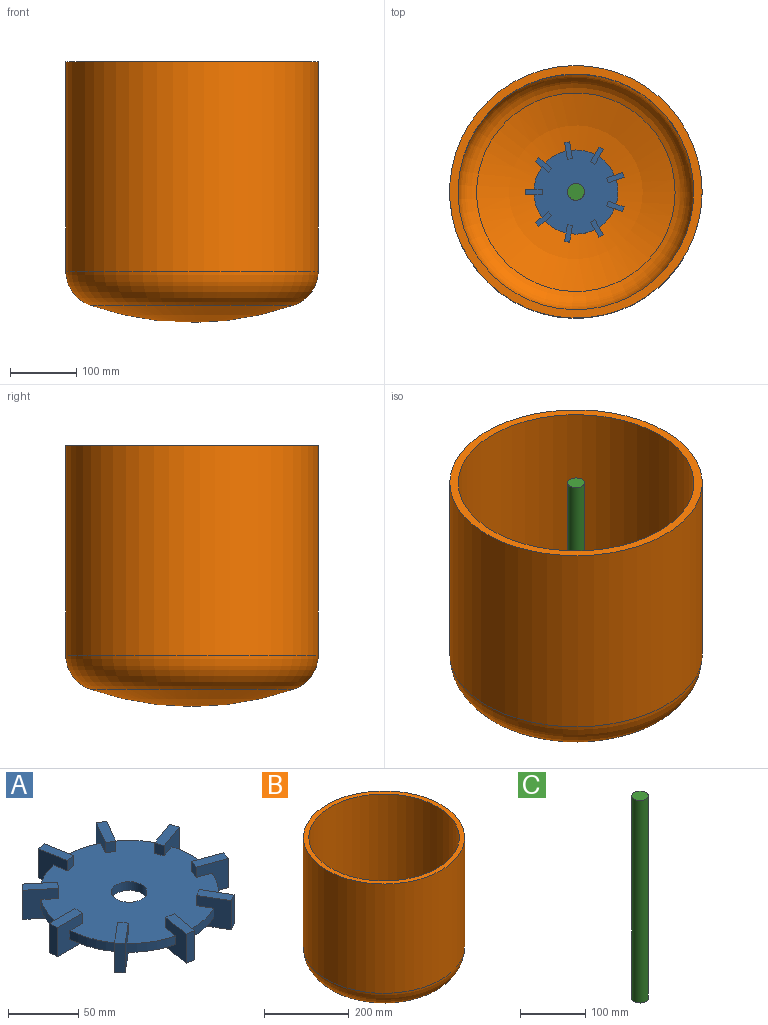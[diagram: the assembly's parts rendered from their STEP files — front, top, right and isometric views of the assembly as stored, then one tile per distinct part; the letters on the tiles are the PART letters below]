
ASSEMBLY  parts=3 mates=2
PART A: 75 faces, bbox 149.1x151.4x25.4 mm
  f0: cylinder r=63.5mm len=34.02mm, axis (0,0,-1), area 279.7mm2, adj f1,f2,f16,f70
  f1: plane 127x126.89mm, normal (0,0,1), area 11292.6mm2, adj f0,f3,f4,f5,f6,f7,f8,f9
  f2: plane 127x126.89mm, normal (0,0,-1), area 11292.6mm2, adj f0,f3,f4,f5,f6,f7,f8,f9
  f3: cylinder r=63.5mm len=31.35mm, axis (0,0,-1), area 279.7mm2, adj f1,f2,f63,f72
  f4: cylinder r=63.5mm len=35.65mm, axis (0,0,-1), area 279.7mm2, adj f1,f2,f56,f65
  f5: cylinder r=63.5mm len=27.73mm, axis (0,0,-1), area 279.7mm2, adj f1,f2,f49,f58
  f6: cylinder r=63.5mm len=36.2mm, axis (0,0,-1), area 279.7mm2, adj f1,f2,f42,f51
  f7: cylinder r=63.5mm len=27.73mm, axis (0,0,-1), area 279.7mm2, adj f1,f2,f35,f44
  f8: cylinder r=63.5mm len=35.65mm, axis (0,0,-1), area 279.7mm2, adj f1,f2,f28,f37
  f9: cylinder r=63.5mm len=31.35mm, axis (0,0,-1), area 279.7mm2, adj f1,f2,f21,f30
  f10: cylinder r=63.5mm len=34.02mm, axis (0,0,-1), area 279.7mm2, adj f1,f2,f14,f23
  f11: cylinder r=12.7mm len=25.4mm, axis (0,0,-1), area 608mm2, adj f1,f2
  f12: plane 8.89x7.62mm, normal (1,0,0), area 67.7mm2, adj f2,f14,f16,f18
  f13: plane 25.4x7.62mm, normal (-1,0,0), area 193.5mm2, adj f14,f16,f17,f18
  f14: plane 25.4x25.4mm, normal (0,-1,0), area 549.3mm2, adj f1,f2,f10,f12,f13,f15,f17,f18
  f15: plane 8.89x7.62mm, normal (1,0,0), area 67.7mm2, adj f1,f14,f16,f17
  f16: plane 25.4x25.4mm, normal (0,1,0), area 549.3mm2, adj f0,f1,f2,f12,f13,f15,f17,f18
  f17: plane 25.4x7.62mm, normal (0,0,1), area 193.5mm2, adj f13,f14,f15,f16
  f18: plane 25.4x7.62mm, normal (0,0,-1), area 193.5mm2, adj f12,f13,f14,f16
  f19: plane 8.89x5.84mm, normal (0.77,0.64,0), area 67.7mm2, adj f2,f21,f23,f25
  f20: plane 25.4x5.84mm, normal (-0.77,-0.64,0), area 193.5mm2, adj f21,f23,f24,f25
  f21: plane 25.4x19.46mm, normal (0.64,-0.77,0), area 549.3mm2, adj f1,f2,f9,f19,f20,f22,f24,f25
  f22: plane 8.89x5.84mm, normal (0.77,0.64,0), area 67.7mm2, adj f1,f21,f23,f24
  f23: plane 25.4x19.46mm, normal (-0.64,0.77,0), area 549.3mm2, adj f1,f2,f10,f19,f20,f22,f24,f25
  f24: plane 24.36x22.16mm, normal (0,0,1), area 193.5mm2, adj f20,f21,f22,f23
  f25: plane 24.36x22.16mm, normal (0,0,-1), area 193.5mm2, adj f19,f20,f21,f23
  f26: plane 8.89x7.5mm, normal (0.17,0.98,0), area 67.7mm2, adj f2,f28,f30,f32
  f27: plane 25.4x7.5mm, normal (-0.17,-0.98,0), area 193.5mm2, adj f28,f30,f31,f32
  f28: plane 25.4x25.01mm, normal (0.98,-0.17,0), area 549.3mm2, adj f1,f2,f8,f26,f27,f29,f31,f32
  f29: plane 8.89x7.5mm, normal (0.17,0.98,0), area 67.7mm2, adj f1,f28,f30,f31
  f30: plane 25.4x25.01mm, normal (-0.98,0.17,0), area 549.3mm2, adj f1,f2,f9,f26,f27,f29,f31,f32
  f31: plane 26.34x11.92mm, normal (0,0,1), area 193.5mm2, adj f27,f28,f29,f30
  f32: plane 26.34x11.92mm, normal (0,0,-1), area 193.5mm2, adj f26,f27,f28,f30
  f33: plane 8.89x6.6mm, normal (-0.5,0.87,0), area 67.7mm2, adj f2,f35,f37,f39
  f34: plane 25.4x6.6mm, normal (0.5,-0.87,0), area 193.5mm2, adj f35,f37,f38,f39
  f35: plane 25.4x22mm, normal (0.87,0.5,0), area 549.3mm2, adj f1,f2,f7,f33,f34,f36,f38,f39
  f36: plane 8.89x6.6mm, normal (-0.5,0.87,0), area 67.7mm2, adj f1,f35,f37,f38
  f37: plane 25.4x22mm, normal (-0.87,-0.5,0), area 549.3mm2, adj f1,f2,f8,f33,f34,f36,f38,f39
  f38: plane 25.81x19.3mm, normal (0,0,1), area 193.5mm2, adj f34,f35,f36,f37
  f39: plane 25.81x19.3mm, normal (0,0,-1), area 193.5mm2, adj f33,f34,f35,f37
  f40: plane 8.89x7.16mm, normal (-0.94,0.34,0), area 67.7mm2, adj f2,f42,f44,f46
  f41: plane 25.4x7.16mm, normal (0.94,-0.34,0), area 193.5mm2, adj f42,f44,f45,f46
  f42: plane 25.4x23.87mm, normal (0.34,0.94,0), area 549.3mm2, adj f1,f2,f6,f40,f41,f43,f45,f46
  f43: plane 8.89x7.16mm, normal (-0.94,0.34,0), area 67.7mm2, adj f1,f42,f44,f45
  f44: plane 25.4x23.87mm, normal (-0.34,-0.94,0), area 549.3mm2, adj f1,f2,f7,f40,f41,f43,f45,f46
  f45: plane 26.47x15.85mm, normal (0,0,1), area 193.5mm2, adj f41,f42,f43,f44
  f46: plane 26.47x15.85mm, normal (0,0,-1), area 193.5mm2, adj f40,f41,f42,f44
  f47: plane 8.89x7.16mm, normal (-0.94,-0.34,0), area 67.7mm2, adj f2,f49,f51,f53
  f48: plane 25.4x7.16mm, normal (0.94,0.34,0), area 193.5mm2, adj f49,f51,f52,f53
  f49: plane 25.4x23.87mm, normal (-0.34,0.94,0), area 549.3mm2, adj f1,f2,f5,f47,f48,f50,f52,f53
  f50: plane 8.89x7.16mm, normal (-0.94,-0.34,0), area 67.7mm2, adj f1,f49,f51,f52
  f51: plane 25.4x23.87mm, normal (0.34,-0.94,0), area 549.3mm2, adj f1,f2,f6,f47,f48,f50,f52,f53
  f52: plane 26.47x15.85mm, normal (0,0,1), area 193.5mm2, adj f48,f49,f50,f51
  f53: plane 26.47x15.85mm, normal (0,0,-1), area 193.5mm2, adj f47,f48,f49,f51
  f54: plane 8.89x6.6mm, normal (-0.5,-0.87,0), area 67.7mm2, adj f2,f56,f58,f60
  f55: plane 25.4x6.6mm, normal (0.5,0.87,0), area 193.5mm2, adj f56,f58,f59,f60
  f56: plane 25.4x22mm, normal (-0.87,0.5,0), area 549.3mm2, adj f1,f2,f4,f54,f55,f57,f59,f60
  f57: plane 8.89x6.6mm, normal (-0.5,-0.87,0), area 67.7mm2, adj f1,f56,f58,f59
  f58: plane 25.4x22mm, normal (0.87,-0.5,0), area 549.3mm2, adj f1,f2,f5,f54,f55,f57,f59,f60
  f59: plane 25.81x19.3mm, normal (0,0,1), area 193.5mm2, adj f55,f56,f57,f58
  f60: plane 25.81x19.3mm, normal (0,0,-1), area 193.5mm2, adj f54,f55,f56,f58
  f61: plane 8.89x7.5mm, normal (0.17,-0.98,0), area 67.7mm2, adj f2,f63,f65,f67
  f62: plane 25.4x7.5mm, normal (-0.17,0.98,0), area 193.5mm2, adj f63,f65,f66,f67
  f63: plane 25.4x25.01mm, normal (-0.98,-0.17,0), area 549.3mm2, adj f1,f2,f3,f61,f62,f64,f66,f67
  f64: plane 8.89x7.5mm, normal (0.17,-0.98,0), area 67.7mm2, adj f1,f63,f65,f66
  f65: plane 25.4x25.01mm, normal (0.98,0.17,0), area 549.3mm2, adj f1,f2,f4,f61,f62,f64,f66,f67
  f66: plane 26.34x11.92mm, normal (0,0,1), area 193.5mm2, adj f62,f63,f64,f65
  f67: plane 26.34x11.92mm, normal (0,0,-1), area 193.5mm2, adj f61,f62,f63,f65
  f68: plane 8.89x5.84mm, normal (0.77,-0.64,0), area 67.7mm2, adj f2,f70,f72,f74
  f69: plane 25.4x5.84mm, normal (-0.77,0.64,0), area 193.5mm2, adj f70,f72,f73,f74
  f70: plane 25.4x19.46mm, normal (-0.64,-0.77,0), area 549.3mm2, adj f0,f1,f2,f68,f69,f71,f73,f74
  f71: plane 8.89x5.84mm, normal (0.77,-0.64,0), area 67.7mm2, adj f1,f70,f72,f73
  f72: plane 25.4x19.46mm, normal (0.64,0.77,0), area 549.3mm2, adj f1,f2,f3,f68,f69,f71,f73,f74
  f73: plane 24.36x22.16mm, normal (0,0,1), area 193.5mm2, adj f69,f70,f71,f72
  f74: plane 24.36x22.16mm, normal (0,0,-1), area 193.5mm2, adj f68,f69,f70,f72
PART B: 7 faces, bbox 412.4x412.4x393.7 mm
  f0: sphere r=468.63mm, area 76527.2mm2, adj f6
  f1: sphere r=455.93mm, area 72435.6mm2, adj f2
  f2: torus R=136mm, axis (0,0,1), area 54527.9mm2, adj f1,f3
  f3: cylinder r=177.8mm len=355.6mm, axis (0,0,1), area 353276.5mm2, adj f2,f4
  f4: plane 381x381mm, normal (0,0,1), area 14694.5mm2, adj f3,f5
  f5: cylinder r=190.5mm len=381mm, axis (0,0,1), area 378510.5mm2, adj f4,f6
  f6: torus R=136mm, axis (0,0,1), area 75201.8mm2, adj f0,f5
PART C: 3 faces, bbox 25.4x25.4x381 mm
  f0: cylinder r=12.7mm len=381mm, axis (0,0,-1), area 30402.4mm2, adj f1,f2
  f1: plane 25.4x25.4mm, normal (0,0,1), area 506.7mm2, adj f0
  f2: plane 25.4x25.4mm, normal (0,0,-1), area 506.7mm2, adj f0
PLACE A t=(22.04,-301.79,-404.08)mm
PLACE B t=(22.04,-301.79,-367.88)mm
PLACE C t=(22.04,-301.79,-476.47)mm
MATE fastened C.f0 <-> B.f2  axis (0,0,1) through (22.04,-301.79,-209.77)mm
MATE fastened A.f0 <-> C.f0  axis (0,0,1) through (22.04,-301.79,-400.27)mm
